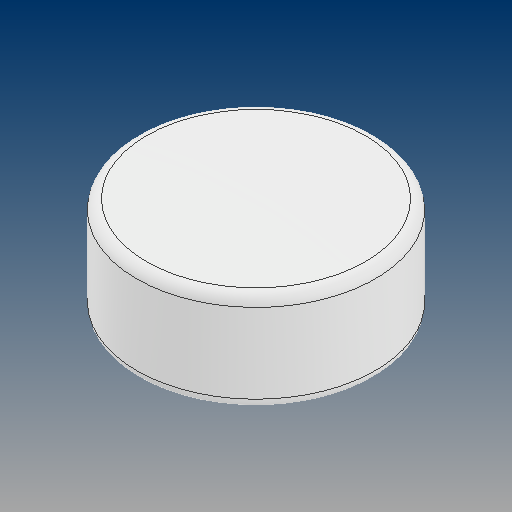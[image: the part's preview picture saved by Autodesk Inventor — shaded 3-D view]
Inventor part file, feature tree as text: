
AUTODESK INVENTOR PART (.ipt)
format: ipt  version: 2024.3 (Build 283343000, 343)  size: 103,424 bytes
history: native  units: in
note: dims shown in document units (in); Inventor stores cm internally (conversion verified against a paired STEP export)
features: fillet x1
ambient origin geometry x8: Origin, YZ Plane, XZ Plane, XY Plane, X Axis, Y Axis, Z Axis, Center Point
bodies: Solid1 (feature_tree)
feature tree (1):
  fillet  "Fillet1"  [1 undecoded]
note: 1 required parameter value undecoded (feature->parameter linkage not recoverable at this tier; creation-order binding heuristic only, values carry confidence <= 0.55)
